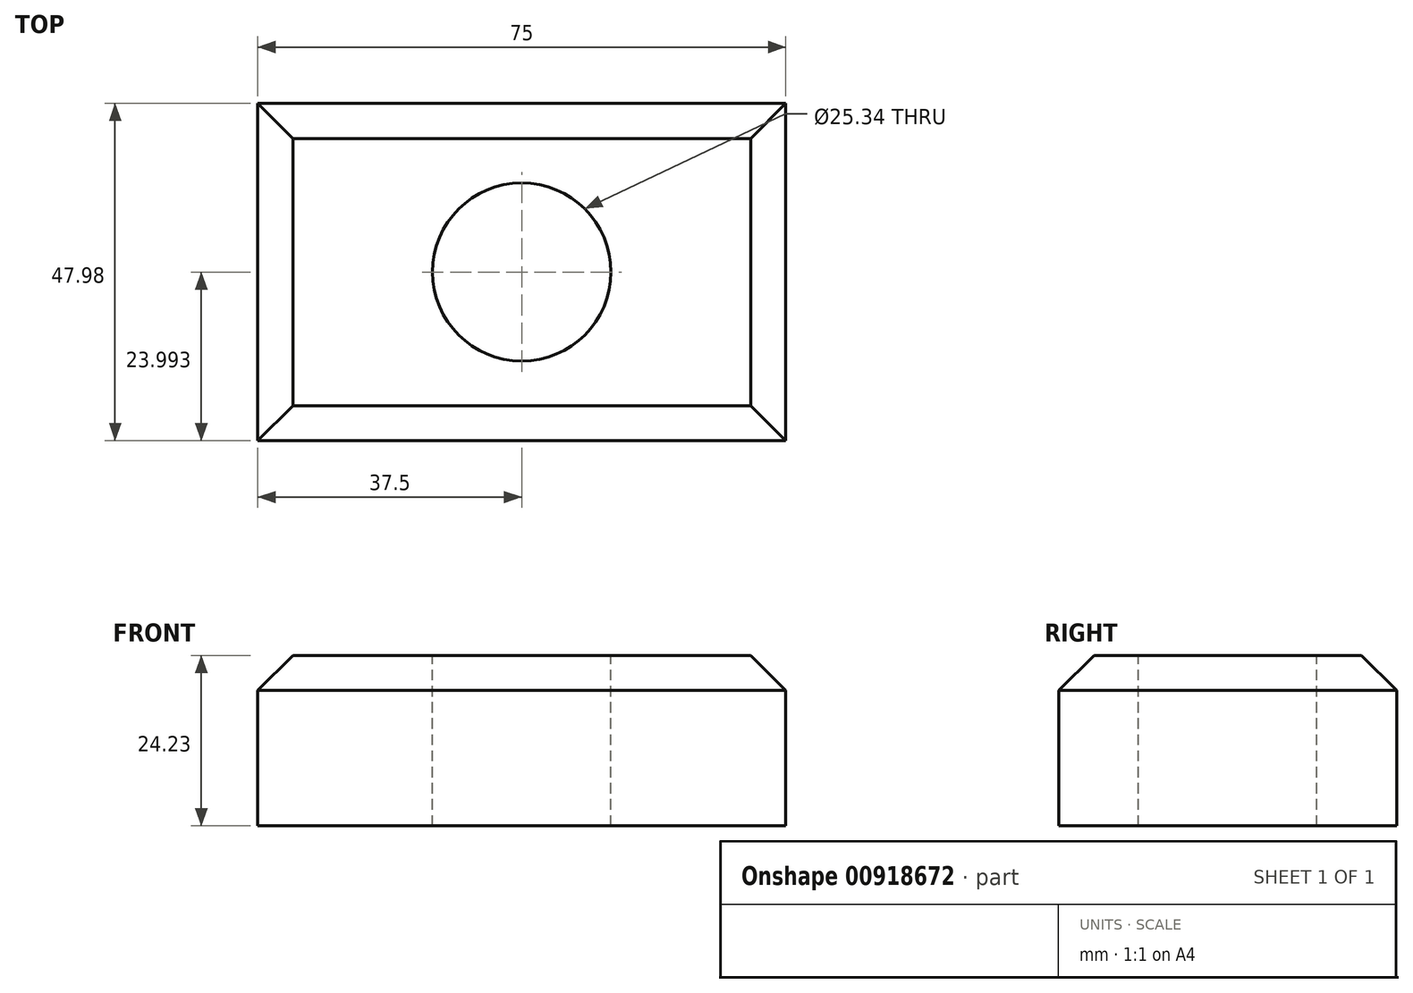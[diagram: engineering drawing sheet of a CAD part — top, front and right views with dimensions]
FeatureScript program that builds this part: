
annotation { "Feature Type Name" : "Feature", "Feature Type Description" : "" }
export const myFeature = defineFeature(function(context is Context, id is Id, definition is map)
    precondition{}
    {
        {
            var Q0;
            Q0=qCreatedBy(makeId("Right.planeOp"),FACE);
            var sketch = newSketch(context, id + "F0", { "sketchPlane" : qUnion([Q0])});
            skLineSegment(sketch, "E0", {"start": v(-68.68, 59.75) * mm, "end": v(-20.7, 59.75) * mm});
            skLineSegment(sketch, "E1", {"start": v(-20.7, 59.75) * mm, "end": v(-20.7, 35.52) * mm});
            skLineSegment(sketch, "E2", {"start": v(-20.7, 35.52) * mm, "end": v(-68.68, 35.52) * mm});
            skLineSegment(sketch, "E3", {"start": v(-68.68, 35.52) * mm, "end": v(-68.68, 59.75) * mm});
            skSolve(sketch);
        }
        {
            var Q0;
            Q0=makeQuery(id+"F0.imprint","IMPRINT",FACE,{"disambiguationData":[TD([[makeQuery(id+"F0.imprint","IMPRINT",EDGE,{"derivedFrom":sQuery(id+"F0.wireOp",EDGE,"E0")}),-1.0]])]});
            extrude(context, id + "F1", {"entities" : qUnion([Q0]), "depth" : 75 * mm, "offsetDistance" : 25 * mm});
        }
        {
            var Q0;
            Q0=makeQuery(id+"F1.opExtrude","SWEPT_EDGE",EDGE,{"disambiguationData":[OSD([sQuery(id+"F0.wireOp",EDGE,"E0"),sQuery(id+"F0.wireOp",EDGE,"E3")])]});
            var Q1;
            Q1=makeQuery(id+"F1.opExtrude","SWEPT_EDGE",EDGE,{"disambiguationData":[OSD([sQuery(id+"F0.wireOp",EDGE,"E0"),sQuery(id+"F0.wireOp",EDGE,"E1")])]});
            var Q2;
            Q2=makeQuery(id+"F1.opExtrude","CAP_EDGE",EDGE,{"disambiguationData":[OSD([sQuery(id+"F0.wireOp",EDGE,"E0")])],"isStart":false});
            var Q3;
            Q3=makeQuery(id+"F1.opExtrude","CAP_EDGE",EDGE,{"disambiguationData":[OSD([sQuery(id+"F0.wireOp",EDGE,"E0")])],"isStart":true});
            chamfer(context, id + "F2", {"entities" : qUnion([Q0, Q1, Q2, Q3]), "width" : 5 * mm, "tangentPropagation" : true});
        }
        {
            var Q0;
            Q0=makeQuery(id+"F1.opExtrude","SWEPT_FACE",FACE,{"disambiguationData":[OSD([sQuery(id+"F0.wireOp",EDGE,"E0")])]});
            var sketch = newSketch(context, id + "F3", { "sketchPlane" : qUnion([Q0])});
            skCircle(sketch, "E4", {"center": v(37.5, -44.69) * mm, "radius": 12.67 * mm});
            skPoint(sketch, "E4.centerSnap0", {"position": v(5, -44.69) * mm});
            skPoint(sketch, "E4.centerSnap1", {"position": v(37.5, -25.7) * mm});
            skSolve(sketch);
        }
        {
            var Q0;
            Q0=makeQuery(id+"F3.imprint","IMPRINT",FACE,{"disambiguationData":[TD([[makeQuery(id+"F3.imprint","IMPRINT",EDGE,{"derivedFrom":sQuery(id+"F3.wireOp",EDGE,"E4")}),1.0]])]});
            extrude(context, id + "F4", {"entities" : qUnion([Q0]), "operationType" : NewBodyOperationType.REMOVE, "endBound" : BoundingType.UP_TO_NEXT, "oppositeDirection" : true, "depth" : 25 * mm, "offsetDistance" : 25 * mm});
        }
    });
